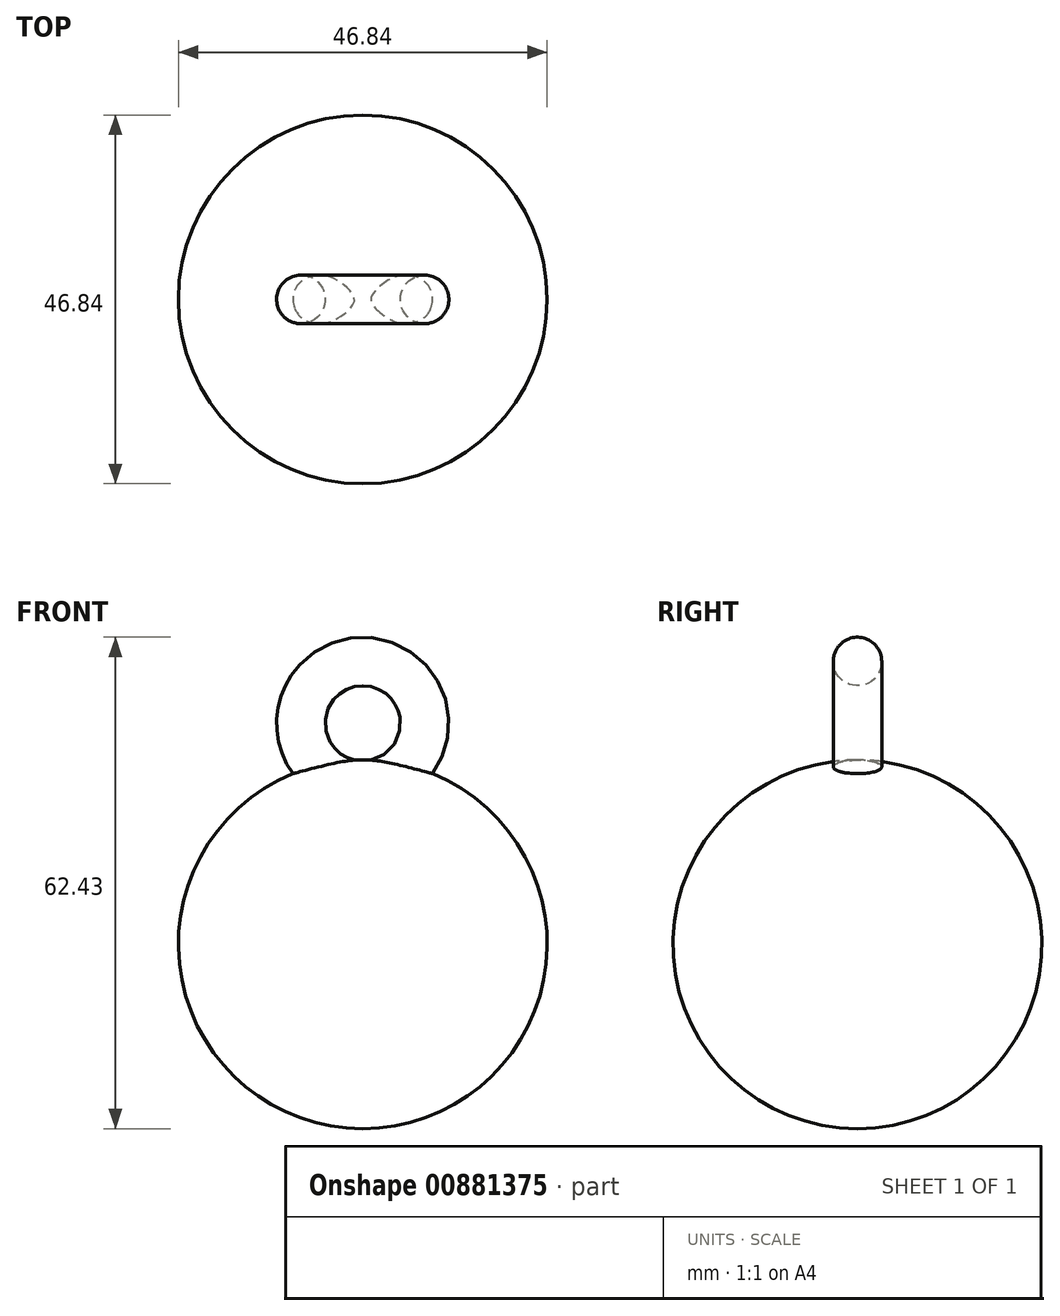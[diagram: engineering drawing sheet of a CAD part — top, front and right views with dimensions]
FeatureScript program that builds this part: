
annotation { "Feature Type Name" : "Feature", "Feature Type Description" : "" }
export const myFeature = defineFeature(function(context is Context, id is Id, definition is map)
    precondition{}
    {
        {
            var Q0;
            Q0=qCreatedBy(makeId("Front.planeOp"),FACE);
            var sketch = newSketch(context, id + "F0", { "sketchPlane" : qUnion([Q0])});
            skArc(sketch, "E0", {"start": v(0, -22.2) * mm, "mid": v(-23.42, 1.23) * mm, "end": v(0, 24.66) * mm});
            skLineSegment(sketch, "E1", {"start": v(0, 37.6) * mm, "end": v(0, -34.52) * mm});
            skSolve(sketch);
        }
        {
            var Q0;
            Q0 = qSketchRegion(id + "F0", true);
            var Q1;
            Q1=sQuery(id+"F0.wireOp",EDGE,"E1");
            revolve(context, id + "F1", {"surfaceOperationType" : NewSurfaceOperationType.NEW, "entities" : qUnion([Q0]), "axis" : qUnion([Q1]), "revolveType" : RevolveType.FULL});
        }
        {
            var Q0;
            Q0=qCreatedBy(makeId("Top.planeOp"),FACE);
            cPlane(context, id + "F2", {"entities" : qUnion([Q0]), "cplaneType" : CPlaneType.OFFSET, "offset" : 29.3 * mm, "width" : 150 * mm, "height" : 150 * mm});
        }
        {
            var Q0;
            Q0=qCreatedBy(id+"F2.planeOp",FACE);
            var sketch = newSketch(context, id + "F3", { "sketchPlane" : qUnion([Q0])});
            skLineSegment(sketch, "E2", {"start": v(0, 11.1) * mm, "end": v(0, -10.48) * mm});
            skCircle(sketch, "E3", {"center": v(-7.86, 0) * mm, "radius": 3.08 * mm});
            skSolve(sketch);
        }
        {
            var Q0;
            Q0 = qSketchRegion(id + "F3", true);
            var Q1;
            Q1=sQuery(id+"F3.wireOp",EDGE,"E2");
            revolve(context, id + "F4", {"operationType" : NewBodyOperationType.ADD, "surfaceOperationType" : NewSurfaceOperationType.NEW, "entities" : qUnion([Q0]), "axis" : qUnion([Q1]), "revolveType" : RevolveType.FULL});
        }
    });
